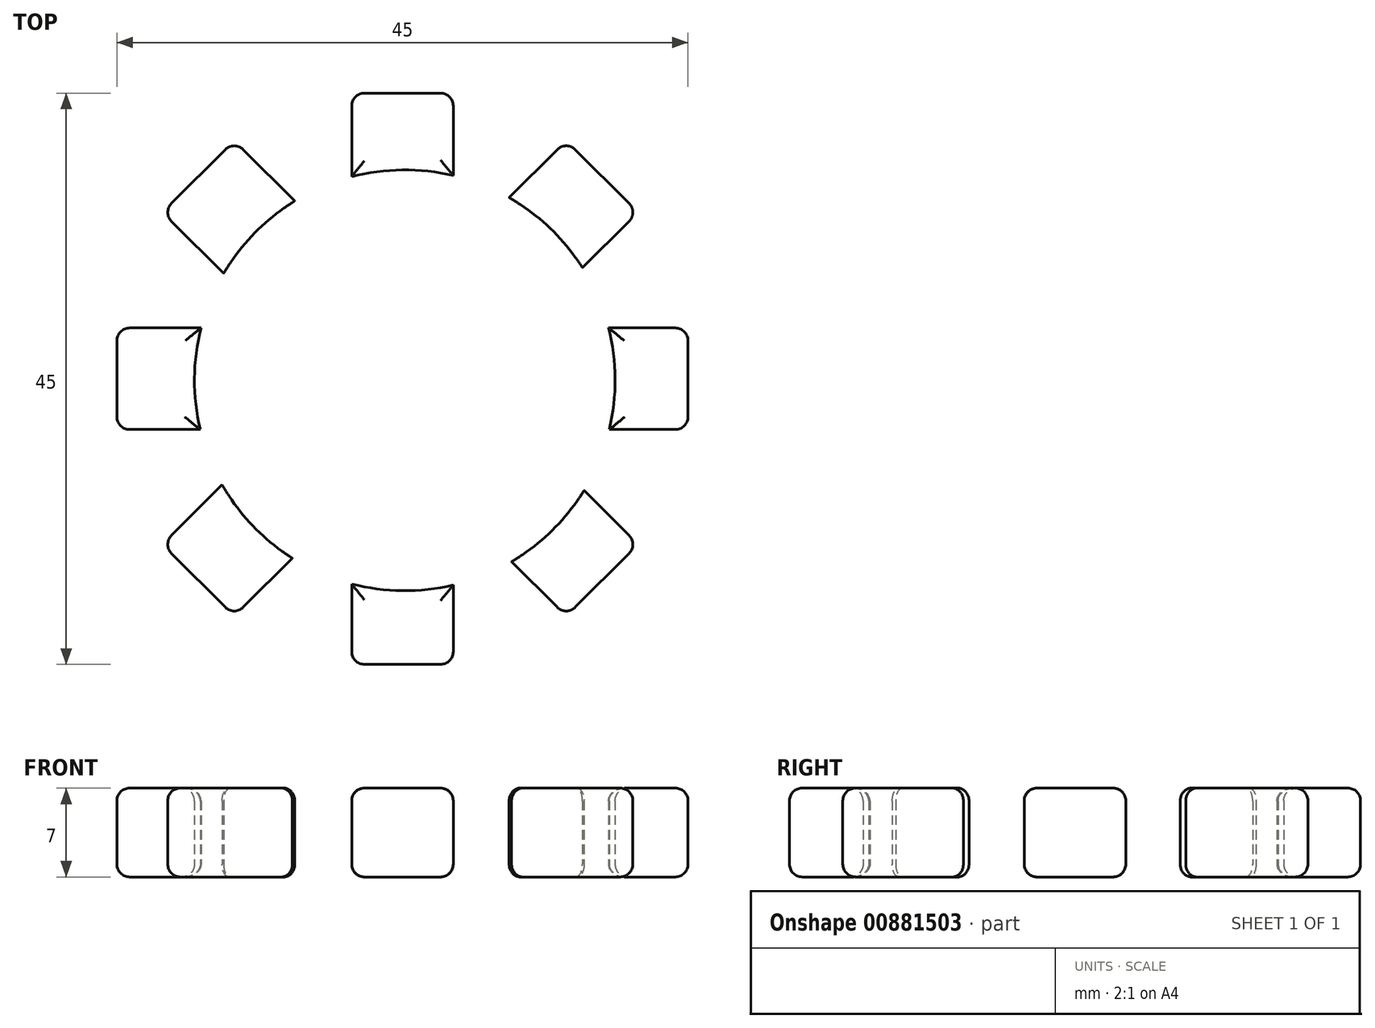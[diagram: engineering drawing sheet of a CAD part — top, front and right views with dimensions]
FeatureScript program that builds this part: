
annotation { "Feature Type Name" : "Feature", "Feature Type Description" : "" }
export const myFeature = defineFeature(function(context is Context, id is Id, definition is map)
    precondition{}
    {
        {
            var Q0;
            Q0=qCreatedBy(makeId("Top.planeOp"),FACE);
            var sketch = newSketch(context, id + "F0", { "sketchPlane" : qUnion([Q0])});
            skLineSegment(sketch, "E0.bottom", {"start": v(4, -22.5) * mm, "end": v(-4, -22.5) * mm});
            skLineSegment(sketch, "E0.top", {"start": v(4, 22.5) * mm, "end": v(-4, 22.5) * mm});
            skLineSegment(sketch, "E0.left", {"start": v(4, -22.5) * mm, "end": v(4, 22.5) * mm});
            skLineSegment(sketch, "E0.right", {"start": v(-4, -22.5) * mm, "end": v(-4, 22.5) * mm});
            skPoint(sketch, "E0.middle", {"position": v(0, 0) * mm});
            skLineSegment(sketch, "E1.bottom", {"start": v(22.5, -4) * mm, "end": v(-22.5, -4) * mm});
            skLineSegment(sketch, "E1.top", {"start": v(22.5, 4) * mm, "end": v(-22.5, 4) * mm});
            skLineSegment(sketch, "E1.left", {"start": v(22.5, -4) * mm, "end": v(22.5, 4) * mm});
            skLineSegment(sketch, "E1.right", {"start": v(-22.5, -4) * mm, "end": v(-22.5, 4) * mm});
            skPoint(sketch, "E2.middle", {"position": v(0.18, -0.13) * mm});
            skLineSegment(sketch, "E3.bottom", {"start": v(18.57, -13.06) * mm, "end": v(12.9, -18.71) * mm});
            skLineSegment(sketch, "E3.top", {"start": v(-13.25, 18.76) * mm, "end": v(-18.91, 13.1) * mm});
            skLineSegment(sketch, "E3.left", {"start": v(18.57, -13.06) * mm, "end": v(-13.25, 18.76) * mm});
            skLineSegment(sketch, "E3.right", {"start": v(12.9, -18.71) * mm, "end": v(-18.91, 13.1) * mm});
            skPoint(sketch, "E3.middle", {"position": v(-0.17, 0.03) * mm});
            skLineSegment(sketch, "E4.bottom", {"start": v(18.57, 13.1) * mm, "end": v(-13.25, -18.71) * mm});
            skLineSegment(sketch, "E4.top", {"start": v(12.9, 18.76) * mm, "end": v(-18.91, -13.06) * mm});
            skLineSegment(sketch, "E4.left", {"start": v(18.57, 13.1) * mm, "end": v(12.9, 18.76) * mm});
            skLineSegment(sketch, "E4.right", {"start": v(-13.25, -18.71) * mm, "end": v(-18.91, -13.06) * mm});
            skPoint(sketch, "E5.middle", {"position": v(0.05, 0.06) * mm});
            skCircle(sketch, "E6", {"center": v(-0.17, 0.03) * mm, "radius": 11.07 * mm});
            skCircle(sketch, "E7", {"center": v(0.18, -0.13) * mm, "radius": 16.57 * mm});
            skSolve(sketch);
        }
        {
            var Q0;
            {var subQ0=sQuery(id+"F0.wireOp",EDGE,"E3.top");Q0=makeQuery(id+"F0.imprint","IMPRINT",FACE,{"disambiguationData":[TD([[makeQuery(id+"F0.imprint","IMPRINT",EDGE,{"derivedFrom":subQ0}),1.0]])]});}
            var Q1;
            {var subQ0=sQuery(id+"F0.wireOp",EDGE,"E7");var subQ1=sQuery(id+"F0.wireOp",EDGE,"E3.left");var subQ2=makeQuery(id+"F0.imprint","INTERSECT",VERTEX,{"disambiguationData":[OD(1.0)],"derivedFrom":[subQ1,subQ0]});Q1=makeQuery(id+"F0.imprint","IMPRINT",FACE,{"disambiguationData":[TD([[makeQuery(id+"F0.imprint","IMPRINT",EDGE,{"disambiguationData":[TD([[subQ2,1.0]])],"derivedFrom":subQ1}),1.0]])]});}
            var Q2;
            {var subQ0=sQuery(id+"F0.wireOp",EDGE,"E7");var subQ1=sQuery(id+"F0.wireOp",EDGE,"E0.right");var subQ2=makeQuery(id+"F0.imprint","INTERSECT",VERTEX,{"disambiguationData":[OD(1.0)],"derivedFrom":[subQ1,subQ0]});Q2=makeQuery(id+"F0.imprint","IMPRINT",FACE,{"disambiguationData":[TD([[makeQuery(id+"F0.imprint","IMPRINT",EDGE,{"disambiguationData":[TD([[subQ2,1.0]])],"derivedFrom":subQ1}),1.0]])]});}
            var Q3;
            {var subQ0=sQuery(id+"F0.wireOp",EDGE,"E7");var subQ1=sQuery(id+"F0.wireOp",EDGE,"E0.left");var subQ2=makeQuery(id+"F0.imprint","INTERSECT",VERTEX,{"disambiguationData":[OD(1.0)],"derivedFrom":[subQ1,subQ0]});Q3=makeQuery(id+"F0.imprint","IMPRINT",FACE,{"disambiguationData":[TD([[makeQuery(id+"F0.imprint","IMPRINT",EDGE,{"disambiguationData":[TD([[subQ2,1.0]])],"derivedFrom":subQ1}),1.0]])]});}
            var Q4;
            {var subQ0=sQuery(id+"F0.wireOp",EDGE,"E0.top");Q4=makeQuery(id+"F0.imprint","IMPRINT",FACE,{"disambiguationData":[TD([[makeQuery(id+"F0.imprint","IMPRINT",EDGE,{"derivedFrom":subQ0}),1.0]])]});}
            var Q5;
            {var subQ0=sQuery(id+"F0.wireOp",EDGE,"E7");var subQ1=sQuery(id+"F0.wireOp",EDGE,"E0.left");var subQ2=makeQuery(id+"F0.imprint","INTERSECT",VERTEX,{"disambiguationData":[OD(1.0)],"derivedFrom":[subQ1,subQ0]});Q5=makeQuery(id+"F0.imprint","IMPRINT",FACE,{"disambiguationData":[TD([[makeQuery(id+"F0.imprint","IMPRINT",EDGE,{"disambiguationData":[TD([[subQ2,1.0]])],"derivedFrom":subQ1}),-1.0]])]});}
            var Q6;
            {var subQ0=sQuery(id+"F0.wireOp",EDGE,"E7");var subQ1=sQuery(id+"F0.wireOp",EDGE,"E4.bottom");var subQ2=makeQuery(id+"F0.imprint","INTERSECT",VERTEX,{"disambiguationData":[OD(0.0)],"derivedFrom":[subQ1,subQ0]});Q6=makeQuery(id+"F0.imprint","IMPRINT",FACE,{"disambiguationData":[TD([[makeQuery(id+"F0.imprint","IMPRINT",EDGE,{"disambiguationData":[TD([[subQ2,-1.0]])],"derivedFrom":subQ1}),-1.0]])]});}
            var Q7;
            {var subQ0=sQuery(id+"F0.wireOp",EDGE,"E4.left");Q7=makeQuery(id+"F0.imprint","IMPRINT",FACE,{"disambiguationData":[TD([[makeQuery(id+"F0.imprint","IMPRINT",EDGE,{"derivedFrom":subQ0}),1.0]])]});}
            var Q8;
            {var subQ0=sQuery(id+"F0.wireOp",EDGE,"E7");var subQ1=sQuery(id+"F0.wireOp",EDGE,"E1.top");var subQ2=makeQuery(id+"F0.imprint","INTERSECT",VERTEX,{"disambiguationData":[OD(0.0)],"derivedFrom":[subQ1,subQ0]});Q8=makeQuery(id+"F0.imprint","IMPRINT",FACE,{"disambiguationData":[TD([[makeQuery(id+"F0.imprint","IMPRINT",EDGE,{"disambiguationData":[TD([[subQ2,-1.0]])],"derivedFrom":subQ1}),-1.0]])]});}
            var Q9;
            {var subQ0=sQuery(id+"F0.wireOp",EDGE,"E7");var subQ1=sQuery(id+"F0.wireOp",EDGE,"E1.bottom");var subQ2=makeQuery(id+"F0.imprint","INTERSECT",VERTEX,{"disambiguationData":[OD(0.0)],"derivedFrom":[subQ1,subQ0]});Q9=makeQuery(id+"F0.imprint","IMPRINT",FACE,{"disambiguationData":[TD([[makeQuery(id+"F0.imprint","IMPRINT",EDGE,{"disambiguationData":[TD([[subQ2,-1.0]])],"derivedFrom":subQ1}),-1.0]])]});}
            var Q10;
            {var subQ0=sQuery(id+"F0.wireOp",EDGE,"E1.left");Q10=makeQuery(id+"F0.imprint","IMPRINT",FACE,{"disambiguationData":[TD([[makeQuery(id+"F0.imprint","IMPRINT",EDGE,{"derivedFrom":subQ0}),1.0]])]});}
            var Q11;
            {var subQ0=sQuery(id+"F0.wireOp",EDGE,"E7");var subQ1=sQuery(id+"F0.wireOp",EDGE,"E1.bottom");var subQ2=makeQuery(id+"F0.imprint","INTERSECT",VERTEX,{"disambiguationData":[OD(0.0)],"derivedFrom":[subQ1,subQ0]});Q11=makeQuery(id+"F0.imprint","IMPRINT",FACE,{"disambiguationData":[TD([[makeQuery(id+"F0.imprint","IMPRINT",EDGE,{"disambiguationData":[TD([[subQ2,-1.0]])],"derivedFrom":subQ1}),1.0]])]});}
            var Q12;
            {var subQ0=sQuery(id+"F0.wireOp",EDGE,"E7");var subQ1=sQuery(id+"F0.wireOp",EDGE,"E3.left");var subQ2=makeQuery(id+"F0.imprint","INTERSECT",VERTEX,{"disambiguationData":[OD(0.0)],"derivedFrom":[subQ1,subQ0]});Q12=makeQuery(id+"F0.imprint","IMPRINT",FACE,{"disambiguationData":[TD([[makeQuery(id+"F0.imprint","IMPRINT",EDGE,{"disambiguationData":[TD([[subQ2,-1.0]])],"derivedFrom":subQ1}),1.0]])]});}
            var Q13;
            {var subQ0=sQuery(id+"F0.wireOp",EDGE,"E3.bottom");Q13=makeQuery(id+"F0.imprint","IMPRINT",FACE,{"disambiguationData":[TD([[makeQuery(id+"F0.imprint","IMPRINT",EDGE,{"derivedFrom":subQ0}),-1.0]])]});}
            var Q14;
            {var subQ0=sQuery(id+"F0.wireOp",EDGE,"E7");var subQ1=sQuery(id+"F0.wireOp",EDGE,"E0.left");var subQ2=makeQuery(id+"F0.imprint","INTERSECT",VERTEX,{"disambiguationData":[OD(0.0)],"derivedFrom":[subQ1,subQ0]});Q14=makeQuery(id+"F0.imprint","IMPRINT",FACE,{"disambiguationData":[TD([[makeQuery(id+"F0.imprint","IMPRINT",EDGE,{"disambiguationData":[TD([[subQ2,-1.0]])],"derivedFrom":subQ1}),1.0]])]});}
            var Q15;
            {var subQ0=sQuery(id+"F0.wireOp",EDGE,"E0.bottom");Q15=makeQuery(id+"F0.imprint","IMPRINT",FACE,{"disambiguationData":[TD([[makeQuery(id+"F0.imprint","IMPRINT",EDGE,{"derivedFrom":subQ0}),-1.0]])]});}
            var Q16;
            {var subQ0=sQuery(id+"F0.wireOp",EDGE,"E7");var subQ1=sQuery(id+"F0.wireOp",EDGE,"E0.left");var subQ2=makeQuery(id+"F0.imprint","INTERSECT",VERTEX,{"disambiguationData":[OD(0.0)],"derivedFrom":[subQ1,subQ0]});Q16=makeQuery(id+"F0.imprint","IMPRINT",FACE,{"disambiguationData":[TD([[makeQuery(id+"F0.imprint","IMPRINT",EDGE,{"disambiguationData":[TD([[subQ2,-1.0]])],"derivedFrom":subQ1}),-1.0]])]});}
            var Q17;
            {var subQ0=sQuery(id+"F0.wireOp",EDGE,"E7");var subQ1=sQuery(id+"F0.wireOp",EDGE,"E0.right");var subQ2=makeQuery(id+"F0.imprint","INTERSECT",VERTEX,{"disambiguationData":[OD(0.0)],"derivedFrom":[subQ1,subQ0]});Q17=makeQuery(id+"F0.imprint","IMPRINT",FACE,{"disambiguationData":[TD([[makeQuery(id+"F0.imprint","IMPRINT",EDGE,{"disambiguationData":[TD([[subQ2,-1.0]])],"derivedFrom":subQ1}),1.0]])]});}
            var Q18;
            {var subQ0=sQuery(id+"F0.wireOp",EDGE,"E7");var subQ1=sQuery(id+"F0.wireOp",EDGE,"E4.bottom");var subQ2=makeQuery(id+"F0.imprint","INTERSECT",VERTEX,{"disambiguationData":[OD(1.0)],"derivedFrom":[subQ1,subQ0]});Q18=makeQuery(id+"F0.imprint","IMPRINT",FACE,{"disambiguationData":[TD([[makeQuery(id+"F0.imprint","IMPRINT",EDGE,{"disambiguationData":[TD([[subQ2,1.0]])],"derivedFrom":subQ1}),-1.0]])]});}
            var Q19;
            {var subQ0=sQuery(id+"F0.wireOp",EDGE,"E4.right");Q19=makeQuery(id+"F0.imprint","IMPRINT",FACE,{"disambiguationData":[TD([[makeQuery(id+"F0.imprint","IMPRINT",EDGE,{"derivedFrom":subQ0}),-1.0]])]});}
            var Q20;
            {var subQ0=sQuery(id+"F0.wireOp",EDGE,"E7");var subQ1=sQuery(id+"F0.wireOp",EDGE,"E1.bottom");var subQ2=makeQuery(id+"F0.imprint","INTERSECT",VERTEX,{"disambiguationData":[OD(1.0)],"derivedFrom":[subQ1,subQ0]});Q20=makeQuery(id+"F0.imprint","IMPRINT",FACE,{"disambiguationData":[TD([[makeQuery(id+"F0.imprint","IMPRINT",EDGE,{"disambiguationData":[TD([[subQ2,1.0]])],"derivedFrom":subQ1}),1.0]])]});}
            var Q21;
            {var subQ0=sQuery(id+"F0.wireOp",EDGE,"E7");var subQ1=sQuery(id+"F0.wireOp",EDGE,"E1.bottom");var subQ2=makeQuery(id+"F0.imprint","INTERSECT",VERTEX,{"disambiguationData":[OD(1.0)],"derivedFrom":[subQ1,subQ0]});Q21=makeQuery(id+"F0.imprint","IMPRINT",FACE,{"disambiguationData":[TD([[makeQuery(id+"F0.imprint","IMPRINT",EDGE,{"disambiguationData":[TD([[subQ2,1.0]])],"derivedFrom":subQ1}),-1.0]])]});}
            var Q22;
            {var subQ0=sQuery(id+"F0.wireOp",EDGE,"E1.right");Q22=makeQuery(id+"F0.imprint","IMPRINT",FACE,{"disambiguationData":[TD([[makeQuery(id+"F0.imprint","IMPRINT",EDGE,{"derivedFrom":subQ0}),-1.0]])]});}
            var Q23;
            {var subQ0=sQuery(id+"F0.wireOp",EDGE,"E7");var subQ1=sQuery(id+"F0.wireOp",EDGE,"E1.top");var subQ2=makeQuery(id+"F0.imprint","INTERSECT",VERTEX,{"disambiguationData":[OD(1.0)],"derivedFrom":[subQ1,subQ0]});Q23=makeQuery(id+"F0.imprint","IMPRINT",FACE,{"disambiguationData":[TD([[makeQuery(id+"F0.imprint","IMPRINT",EDGE,{"disambiguationData":[TD([[subQ2,1.0]])],"derivedFrom":subQ1}),-1.0]])]});}
            extrude(context, id + "F1", {"entities" : qUnion([Q0, Q1, Q2, Q3, Q4, Q5, Q6, Q7, Q8, Q9, Q10, Q11, Q12, Q13, Q14, Q15, Q16, Q17, Q18, Q19, Q20, Q21, Q22, Q23]), "depth" : 7 * mm, "offsetDistance" : 25 * mm});
        }
        {
            var Q0;
            {var subQ0=sQuery(id+"F0.wireOp",EDGE,"E3.left");Q0=makeQuery(id+"F1.opExtrude","CAP_EDGE",EDGE,{"disambiguationData":[OSD([subQ0]),TDD([makeQuery(id+"F0.imprint","IMPRINT",EDGE,{"disambiguationData":[TD([[makeQuery(id+"F0.imprint","INTERSECT",VERTEX,{"derivedFrom":[sQuery(id+"F0.wireOp",EDGE,"E3.top"),subQ0]}),1.0]])],"derivedFrom":subQ0})])],"isStart":false});}
            var Q1;
            {var subQ0=sQuery(id+"F0.wireOp",EDGE,"E7");Q1=makeQuery(id+"F1.opExtrude","CAP_EDGE",EDGE,{"disambiguationData":[OSD([subQ0]),TDD([makeQuery(id+"F0.imprint","IMPRINT",EDGE,{"disambiguationData":[TD([[makeQuery(id+"F0.imprint","INTERSECT",VERTEX,{"disambiguationData":[OD(1.0)],"derivedFrom":[sQuery(id+"F0.wireOp",EDGE,"E0.right"),subQ0]}),-1.0]])],"derivedFrom":subQ0})])],"isStart":false});}
            var Q2;
            {var subQ0=sQuery(id+"F0.wireOp",EDGE,"E0.right");Q2=makeQuery(id+"F1.opExtrude","CAP_EDGE",EDGE,{"disambiguationData":[OSD([subQ0]),TDD([makeQuery(id+"F0.imprint","IMPRINT",EDGE,{"disambiguationData":[TD([[makeQuery(id+"F0.imprint","INTERSECT",VERTEX,{"derivedFrom":[sQuery(id+"F0.wireOp",EDGE,"E0.top"),subQ0]}),1.0]])],"derivedFrom":subQ0})])],"isStart":false});}
            var Q3;
            {var subQ0=sQuery(id+"F0.wireOp",EDGE,"E0.left");Q3=makeQuery(id+"F1.opExtrude","CAP_EDGE",EDGE,{"disambiguationData":[OSD([subQ0]),TDD([makeQuery(id+"F0.imprint","IMPRINT",EDGE,{"disambiguationData":[TD([[makeQuery(id+"F0.imprint","INTERSECT",VERTEX,{"derivedFrom":[sQuery(id+"F0.wireOp",EDGE,"E0.top"),subQ0]}),1.0]])],"derivedFrom":subQ0})])],"isStart":false});}
            var Q4;
            {var subQ0=sQuery(id+"F0.wireOp",EDGE,"E7");Q4=makeQuery(id+"F1.opExtrude","CAP_EDGE",EDGE,{"disambiguationData":[OSD([subQ0]),TDD([makeQuery(id+"F0.imprint","IMPRINT",EDGE,{"disambiguationData":[TD([[makeQuery(id+"F0.imprint","INTERSECT",VERTEX,{"disambiguationData":[OD(1.0)],"derivedFrom":[sQuery(id+"F0.wireOp",EDGE,"E0.left"),subQ0]}),1.0]])],"derivedFrom":subQ0})])],"isStart":false});}
            var Q5;
            {var subQ0=sQuery(id+"F0.wireOp",EDGE,"E4.top");Q5=makeQuery(id+"F1.opExtrude","CAP_EDGE",EDGE,{"disambiguationData":[OSD([subQ0]),TDD([makeQuery(id+"F0.imprint","IMPRINT",EDGE,{"disambiguationData":[TD([[makeQuery(id+"F0.imprint","INTERSECT",VERTEX,{"derivedFrom":[subQ0,sQuery(id+"F0.wireOp",EDGE,"E4.left")]}),-1.0]])],"derivedFrom":subQ0})])],"isStart":false});}
            var Q6;
            {var subQ0=sQuery(id+"F0.wireOp",EDGE,"E4.bottom");Q6=makeQuery(id+"F1.opExtrude","CAP_EDGE",EDGE,{"disambiguationData":[OSD([subQ0]),TDD([makeQuery(id+"F0.imprint","IMPRINT",EDGE,{"disambiguationData":[TD([[makeQuery(id+"F0.imprint","INTERSECT",VERTEX,{"derivedFrom":[subQ0,sQuery(id+"F0.wireOp",EDGE,"E4.left")]}),-1.0]])],"derivedFrom":subQ0})])],"isStart":false});}
            var Q7;
            {var subQ0=sQuery(id+"F0.wireOp",EDGE,"E1.top");Q7=makeQuery(id+"F1.opExtrude","CAP_EDGE",EDGE,{"disambiguationData":[OSD([subQ0]),TDD([makeQuery(id+"F0.imprint","IMPRINT",EDGE,{"disambiguationData":[TD([[makeQuery(id+"F0.imprint","INTERSECT",VERTEX,{"derivedFrom":[subQ0,sQuery(id+"F0.wireOp",EDGE,"E1.left")]}),-1.0]])],"derivedFrom":subQ0})])],"isStart":false});}
            var Q8;
            {var subQ0=sQuery(id+"F0.wireOp",EDGE,"E1.bottom");Q8=makeQuery(id+"F1.opExtrude","CAP_EDGE",EDGE,{"disambiguationData":[OSD([subQ0]),TDD([makeQuery(id+"F0.imprint","IMPRINT",EDGE,{"disambiguationData":[TD([[makeQuery(id+"F0.imprint","INTERSECT",VERTEX,{"derivedFrom":[subQ0,sQuery(id+"F0.wireOp",EDGE,"E1.left")]}),-1.0]])],"derivedFrom":subQ0})])],"isStart":false});}
            var Q9;
            {var subQ0=sQuery(id+"F0.wireOp",EDGE,"E7");Q9=makeQuery(id+"F1.opExtrude","CAP_EDGE",EDGE,{"disambiguationData":[OSD([subQ0]),TDD([makeQuery(id+"F0.imprint","IMPRINT",EDGE,{"disambiguationData":[TD([[makeQuery(id+"F0.imprint","INTERSECT",VERTEX,{"disambiguationData":[OD(0.0)],"derivedFrom":[sQuery(id+"F0.wireOp",EDGE,"E1.top"),subQ0]}),-1.0]])],"derivedFrom":subQ0})])],"isStart":false});}
            var Q10;
            {var subQ0=sQuery(id+"F0.wireOp",EDGE,"E7");Q10=makeQuery(id+"F1.opExtrude","CAP_EDGE",EDGE,{"disambiguationData":[OSD([subQ0]),TDD([makeQuery(id+"F0.imprint","IMPRINT",EDGE,{"disambiguationData":[TD([[makeQuery(id+"F0.imprint","INTERSECT",VERTEX,{"disambiguationData":[OD(0.0)],"derivedFrom":[sQuery(id+"F0.wireOp",EDGE,"E1.bottom"),subQ0]}),1.0]])],"derivedFrom":subQ0})])],"isStart":false});}
            var Q11;
            {var subQ0=sQuery(id+"F0.wireOp",EDGE,"E3.left");Q11=makeQuery(id+"F1.opExtrude","CAP_EDGE",EDGE,{"disambiguationData":[OSD([subQ0]),TDD([makeQuery(id+"F0.imprint","IMPRINT",EDGE,{"disambiguationData":[TD([[makeQuery(id+"F0.imprint","INTERSECT",VERTEX,{"derivedFrom":[sQuery(id+"F0.wireOp",EDGE,"E3.bottom"),subQ0]}),-1.0]])],"derivedFrom":subQ0})])],"isStart":false});}
            var Q12;
            {var subQ0=sQuery(id+"F0.wireOp",EDGE,"E3.right");Q12=makeQuery(id+"F1.opExtrude","CAP_EDGE",EDGE,{"disambiguationData":[OSD([subQ0]),TDD([makeQuery(id+"F0.imprint","IMPRINT",EDGE,{"disambiguationData":[TD([[makeQuery(id+"F0.imprint","INTERSECT",VERTEX,{"derivedFrom":[sQuery(id+"F0.wireOp",EDGE,"E3.bottom"),subQ0]}),-1.0]])],"derivedFrom":subQ0})])],"isStart":false});}
            var Q13;
            {var subQ0=sQuery(id+"F0.wireOp",EDGE,"E7");Q13=makeQuery(id+"F1.opExtrude","CAP_EDGE",EDGE,{"disambiguationData":[OSD([subQ0]),TDD([makeQuery(id+"F0.imprint","IMPRINT",EDGE,{"disambiguationData":[TD([[makeQuery(id+"F0.imprint","INTERSECT",VERTEX,{"disambiguationData":[OD(0.0)],"derivedFrom":[sQuery(id+"F0.wireOp",EDGE,"E0.left"),subQ0]}),-1.0]])],"derivedFrom":subQ0})])],"isStart":false});}
            var Q14;
            {var subQ0=sQuery(id+"F0.wireOp",EDGE,"E0.left");Q14=makeQuery(id+"F1.opExtrude","CAP_EDGE",EDGE,{"disambiguationData":[OSD([subQ0]),TDD([makeQuery(id+"F0.imprint","IMPRINT",EDGE,{"disambiguationData":[TD([[makeQuery(id+"F0.imprint","INTERSECT",VERTEX,{"derivedFrom":[sQuery(id+"F0.wireOp",EDGE,"E0.bottom"),subQ0]}),-1.0]])],"derivedFrom":subQ0})])],"isStart":false});}
            var Q15;
            {var subQ0=sQuery(id+"F0.wireOp",EDGE,"E0.right");Q15=makeQuery(id+"F1.opExtrude","CAP_EDGE",EDGE,{"disambiguationData":[OSD([subQ0]),TDD([makeQuery(id+"F0.imprint","IMPRINT",EDGE,{"disambiguationData":[TD([[makeQuery(id+"F0.imprint","INTERSECT",VERTEX,{"derivedFrom":[sQuery(id+"F0.wireOp",EDGE,"E0.bottom"),subQ0]}),-1.0]])],"derivedFrom":subQ0})])],"isStart":false});}
            var Q16;
            {var subQ0=sQuery(id+"F0.wireOp",EDGE,"E7");Q16=makeQuery(id+"F1.opExtrude","CAP_EDGE",EDGE,{"disambiguationData":[OSD([subQ0]),TDD([makeQuery(id+"F0.imprint","IMPRINT",EDGE,{"disambiguationData":[TD([[makeQuery(id+"F0.imprint","INTERSECT",VERTEX,{"disambiguationData":[OD(0.0)],"derivedFrom":[sQuery(id+"F0.wireOp",EDGE,"E0.right"),subQ0]}),1.0]])],"derivedFrom":subQ0})])],"isStart":false});}
            var Q17;
            {var subQ0=sQuery(id+"F0.wireOp",EDGE,"E4.bottom");Q17=makeQuery(id+"F1.opExtrude","CAP_EDGE",EDGE,{"disambiguationData":[OSD([subQ0]),TDD([makeQuery(id+"F0.imprint","IMPRINT",EDGE,{"disambiguationData":[TD([[makeQuery(id+"F0.imprint","INTERSECT",VERTEX,{"derivedFrom":[subQ0,sQuery(id+"F0.wireOp",EDGE,"E4.right")]}),1.0]])],"derivedFrom":subQ0})])],"isStart":false});}
            var Q18;
            {var subQ0=sQuery(id+"F0.wireOp",EDGE,"E4.top");Q18=makeQuery(id+"F1.opExtrude","CAP_EDGE",EDGE,{"disambiguationData":[OSD([subQ0]),TDD([makeQuery(id+"F0.imprint","IMPRINT",EDGE,{"disambiguationData":[TD([[makeQuery(id+"F0.imprint","INTERSECT",VERTEX,{"derivedFrom":[subQ0,sQuery(id+"F0.wireOp",EDGE,"E4.right")]}),1.0]])],"derivedFrom":subQ0})])],"isStart":false});}
            var Q19;
            {var subQ0=sQuery(id+"F0.wireOp",EDGE,"E7");Q19=makeQuery(id+"F1.opExtrude","CAP_EDGE",EDGE,{"disambiguationData":[OSD([subQ0]),TDD([makeQuery(id+"F0.imprint","IMPRINT",EDGE,{"disambiguationData":[TD([[makeQuery(id+"F0.imprint","INTERSECT",VERTEX,{"disambiguationData":[OD(1.0)],"derivedFrom":[sQuery(id+"F0.wireOp",EDGE,"E1.bottom"),subQ0]}),-1.0]])],"derivedFrom":subQ0})])],"isStart":false});}
            var Q20;
            {var subQ0=sQuery(id+"F0.wireOp",EDGE,"E1.bottom");Q20=makeQuery(id+"F1.opExtrude","CAP_EDGE",EDGE,{"disambiguationData":[OSD([subQ0]),TDD([makeQuery(id+"F0.imprint","IMPRINT",EDGE,{"disambiguationData":[TD([[makeQuery(id+"F0.imprint","INTERSECT",VERTEX,{"derivedFrom":[subQ0,sQuery(id+"F0.wireOp",EDGE,"E1.right")]}),1.0]])],"derivedFrom":subQ0})])],"isStart":false});}
            var Q21;
            {var subQ0=sQuery(id+"F0.wireOp",EDGE,"E1.top");Q21=makeQuery(id+"F1.opExtrude","CAP_EDGE",EDGE,{"disambiguationData":[OSD([subQ0]),TDD([makeQuery(id+"F0.imprint","IMPRINT",EDGE,{"disambiguationData":[TD([[makeQuery(id+"F0.imprint","INTERSECT",VERTEX,{"derivedFrom":[subQ0,sQuery(id+"F0.wireOp",EDGE,"E1.right")]}),1.0]])],"derivedFrom":subQ0})])],"isStart":false});}
            var Q22;
            {var subQ0=sQuery(id+"F0.wireOp",EDGE,"E7");Q22=makeQuery(id+"F1.opExtrude","CAP_EDGE",EDGE,{"disambiguationData":[OSD([subQ0]),TDD([makeQuery(id+"F0.imprint","IMPRINT",EDGE,{"disambiguationData":[TD([[makeQuery(id+"F0.imprint","INTERSECT",VERTEX,{"disambiguationData":[OD(1.0)],"derivedFrom":[sQuery(id+"F0.wireOp",EDGE,"E1.top"),subQ0]}),1.0]])],"derivedFrom":subQ0})])],"isStart":false});}
            var Q23;
            {var subQ0=sQuery(id+"F0.wireOp",EDGE,"E3.right");Q23=makeQuery(id+"F1.opExtrude","CAP_EDGE",EDGE,{"disambiguationData":[OSD([subQ0]),TDD([makeQuery(id+"F0.imprint","IMPRINT",EDGE,{"disambiguationData":[TD([[makeQuery(id+"F0.imprint","INTERSECT",VERTEX,{"derivedFrom":[sQuery(id+"F0.wireOp",EDGE,"E3.top"),subQ0]}),1.0]])],"derivedFrom":subQ0})])],"isStart":false});}
            fillet(context, id + "F2", {"entities" : qUnion([Q0, Q1, Q2, Q3, Q4, Q5, Q6, Q7, Q8, Q9, Q10, Q11, Q12, Q13, Q14, Q15, Q16, Q17, Q18, Q19, Q20, Q21, Q22, Q23]), "radius" : 1 * mm, "tangentPropagation" : true, "allowEdgeOverflow" : false});
        }
        {
            var Q0;
            {var subQ0=sQuery(id+"F0.wireOp",EDGE,"E3.left");Q0=makeQuery(id+"F1.opExtrude","CAP_EDGE",EDGE,{"disambiguationData":[OSD([subQ0]),TDD([makeQuery(id+"F0.imprint","IMPRINT",EDGE,{"disambiguationData":[TD([[makeQuery(id+"F0.imprint","INTERSECT",VERTEX,{"derivedFrom":[sQuery(id+"F0.wireOp",EDGE,"E3.bottom"),subQ0]}),-1.0]])],"derivedFrom":subQ0})])],"isStart":true});}
            var Q1;
            {var subQ0=sQuery(id+"F0.wireOp",EDGE,"E3.right");Q1=makeQuery(id+"F1.opExtrude","CAP_EDGE",EDGE,{"disambiguationData":[OSD([subQ0]),TDD([makeQuery(id+"F0.imprint","IMPRINT",EDGE,{"disambiguationData":[TD([[makeQuery(id+"F0.imprint","INTERSECT",VERTEX,{"derivedFrom":[sQuery(id+"F0.wireOp",EDGE,"E3.bottom"),subQ0]}),-1.0]])],"derivedFrom":subQ0})])],"isStart":true});}
            var Q2;
            {var subQ0=sQuery(id+"F0.wireOp",EDGE,"E7");Q2=makeQuery(id+"F1.opExtrude","CAP_EDGE",EDGE,{"disambiguationData":[OSD([subQ0]),TDD([makeQuery(id+"F0.imprint","IMPRINT",EDGE,{"disambiguationData":[TD([[makeQuery(id+"F0.imprint","INTERSECT",VERTEX,{"disambiguationData":[OD(0.0)],"derivedFrom":[sQuery(id+"F0.wireOp",EDGE,"E1.bottom"),subQ0]}),1.0]])],"derivedFrom":subQ0})])],"isStart":true});}
            var Q3;
            {var subQ0=sQuery(id+"F0.wireOp",EDGE,"E7");Q3=makeQuery(id+"F1.opExtrude","CAP_EDGE",EDGE,{"disambiguationData":[OSD([subQ0]),TDD([makeQuery(id+"F0.imprint","IMPRINT",EDGE,{"disambiguationData":[TD([[makeQuery(id+"F0.imprint","INTERSECT",VERTEX,{"disambiguationData":[OD(0.0)],"derivedFrom":[sQuery(id+"F0.wireOp",EDGE,"E0.left"),subQ0]}),-1.0]])],"derivedFrom":subQ0})])],"isStart":true});}
            var Q4;
            {var subQ0=sQuery(id+"F0.wireOp",EDGE,"E0.left");Q4=makeQuery(id+"F1.opExtrude","CAP_EDGE",EDGE,{"disambiguationData":[OSD([subQ0]),TDD([makeQuery(id+"F0.imprint","IMPRINT",EDGE,{"disambiguationData":[TD([[makeQuery(id+"F0.imprint","INTERSECT",VERTEX,{"derivedFrom":[sQuery(id+"F0.wireOp",EDGE,"E0.bottom"),subQ0]}),-1.0]])],"derivedFrom":subQ0})])],"isStart":true});}
            var Q5;
            {var subQ0=sQuery(id+"F0.wireOp",EDGE,"E0.right");Q5=makeQuery(id+"F1.opExtrude","CAP_EDGE",EDGE,{"disambiguationData":[OSD([subQ0]),TDD([makeQuery(id+"F0.imprint","IMPRINT",EDGE,{"disambiguationData":[TD([[makeQuery(id+"F0.imprint","INTERSECT",VERTEX,{"derivedFrom":[sQuery(id+"F0.wireOp",EDGE,"E0.bottom"),subQ0]}),-1.0]])],"derivedFrom":subQ0})])],"isStart":true});}
            var Q6;
            {var subQ0=sQuery(id+"F0.wireOp",EDGE,"E7");Q6=makeQuery(id+"F1.opExtrude","CAP_EDGE",EDGE,{"disambiguationData":[OSD([subQ0]),TDD([makeQuery(id+"F0.imprint","IMPRINT",EDGE,{"disambiguationData":[TD([[makeQuery(id+"F0.imprint","INTERSECT",VERTEX,{"disambiguationData":[OD(0.0)],"derivedFrom":[sQuery(id+"F0.wireOp",EDGE,"E0.right"),subQ0]}),1.0]])],"derivedFrom":subQ0})])],"isStart":true});}
            var Q7;
            {var subQ0=sQuery(id+"F0.wireOp",EDGE,"E4.bottom");Q7=makeQuery(id+"F1.opExtrude","CAP_EDGE",EDGE,{"disambiguationData":[OSD([subQ0]),TDD([makeQuery(id+"F0.imprint","IMPRINT",EDGE,{"disambiguationData":[TD([[makeQuery(id+"F0.imprint","INTERSECT",VERTEX,{"derivedFrom":[subQ0,sQuery(id+"F0.wireOp",EDGE,"E4.right")]}),1.0]])],"derivedFrom":subQ0})])],"isStart":true});}
            var Q8;
            {var subQ0=sQuery(id+"F0.wireOp",EDGE,"E4.top");Q8=makeQuery(id+"F1.opExtrude","CAP_EDGE",EDGE,{"disambiguationData":[OSD([subQ0]),TDD([makeQuery(id+"F0.imprint","IMPRINT",EDGE,{"disambiguationData":[TD([[makeQuery(id+"F0.imprint","INTERSECT",VERTEX,{"derivedFrom":[subQ0,sQuery(id+"F0.wireOp",EDGE,"E4.right")]}),1.0]])],"derivedFrom":subQ0})])],"isStart":true});}
            var Q9;
            {var subQ0=sQuery(id+"F0.wireOp",EDGE,"E7");Q9=makeQuery(id+"F1.opExtrude","CAP_EDGE",EDGE,{"disambiguationData":[OSD([subQ0]),TDD([makeQuery(id+"F0.imprint","IMPRINT",EDGE,{"disambiguationData":[TD([[makeQuery(id+"F0.imprint","INTERSECT",VERTEX,{"disambiguationData":[OD(1.0)],"derivedFrom":[sQuery(id+"F0.wireOp",EDGE,"E1.bottom"),subQ0]}),-1.0]])],"derivedFrom":subQ0})])],"isStart":true});}
            var Q10;
            {var subQ0=sQuery(id+"F0.wireOp",EDGE,"E1.bottom");Q10=makeQuery(id+"F1.opExtrude","CAP_EDGE",EDGE,{"disambiguationData":[OSD([subQ0]),TDD([makeQuery(id+"F0.imprint","IMPRINT",EDGE,{"disambiguationData":[TD([[makeQuery(id+"F0.imprint","INTERSECT",VERTEX,{"derivedFrom":[subQ0,sQuery(id+"F0.wireOp",EDGE,"E1.right")]}),1.0]])],"derivedFrom":subQ0})])],"isStart":true});}
            var Q11;
            {var subQ0=sQuery(id+"F0.wireOp",EDGE,"E1.top");Q11=makeQuery(id+"F1.opExtrude","CAP_EDGE",EDGE,{"disambiguationData":[OSD([subQ0]),TDD([makeQuery(id+"F0.imprint","IMPRINT",EDGE,{"disambiguationData":[TD([[makeQuery(id+"F0.imprint","INTERSECT",VERTEX,{"derivedFrom":[subQ0,sQuery(id+"F0.wireOp",EDGE,"E1.right")]}),1.0]])],"derivedFrom":subQ0})])],"isStart":true});}
            var Q12;
            {var subQ0=sQuery(id+"F0.wireOp",EDGE,"E7");Q12=makeQuery(id+"F1.opExtrude","CAP_EDGE",EDGE,{"disambiguationData":[OSD([subQ0]),TDD([makeQuery(id+"F0.imprint","IMPRINT",EDGE,{"disambiguationData":[TD([[makeQuery(id+"F0.imprint","INTERSECT",VERTEX,{"disambiguationData":[OD(1.0)],"derivedFrom":[sQuery(id+"F0.wireOp",EDGE,"E1.top"),subQ0]}),1.0]])],"derivedFrom":subQ0})])],"isStart":true});}
            var Q13;
            {var subQ0=sQuery(id+"F0.wireOp",EDGE,"E3.right");Q13=makeQuery(id+"F1.opExtrude","CAP_EDGE",EDGE,{"disambiguationData":[OSD([subQ0]),TDD([makeQuery(id+"F0.imprint","IMPRINT",EDGE,{"disambiguationData":[TD([[makeQuery(id+"F0.imprint","INTERSECT",VERTEX,{"derivedFrom":[sQuery(id+"F0.wireOp",EDGE,"E3.top"),subQ0]}),1.0]])],"derivedFrom":subQ0})])],"isStart":true});}
            var Q14;
            {var subQ0=sQuery(id+"F0.wireOp",EDGE,"E3.left");Q14=makeQuery(id+"F1.opExtrude","CAP_EDGE",EDGE,{"disambiguationData":[OSD([subQ0]),TDD([makeQuery(id+"F0.imprint","IMPRINT",EDGE,{"disambiguationData":[TD([[makeQuery(id+"F0.imprint","INTERSECT",VERTEX,{"derivedFrom":[sQuery(id+"F0.wireOp",EDGE,"E3.top"),subQ0]}),1.0]])],"derivedFrom":subQ0})])],"isStart":true});}
            var Q15;
            {var subQ0=sQuery(id+"F0.wireOp",EDGE,"E7");Q15=makeQuery(id+"F1.opExtrude","CAP_EDGE",EDGE,{"disambiguationData":[OSD([subQ0]),TDD([makeQuery(id+"F0.imprint","IMPRINT",EDGE,{"disambiguationData":[TD([[makeQuery(id+"F0.imprint","INTERSECT",VERTEX,{"disambiguationData":[OD(1.0)],"derivedFrom":[sQuery(id+"F0.wireOp",EDGE,"E0.right"),subQ0]}),-1.0]])],"derivedFrom":subQ0})])],"isStart":true});}
            var Q16;
            {var subQ0=sQuery(id+"F0.wireOp",EDGE,"E0.right");Q16=makeQuery(id+"F1.opExtrude","CAP_EDGE",EDGE,{"disambiguationData":[OSD([subQ0]),TDD([makeQuery(id+"F0.imprint","IMPRINT",EDGE,{"disambiguationData":[TD([[makeQuery(id+"F0.imprint","INTERSECT",VERTEX,{"derivedFrom":[sQuery(id+"F0.wireOp",EDGE,"E0.top"),subQ0]}),1.0]])],"derivedFrom":subQ0})])],"isStart":true});}
            var Q17;
            {var subQ0=sQuery(id+"F0.wireOp",EDGE,"E0.left");Q17=makeQuery(id+"F1.opExtrude","CAP_EDGE",EDGE,{"disambiguationData":[OSD([subQ0]),TDD([makeQuery(id+"F0.imprint","IMPRINT",EDGE,{"disambiguationData":[TD([[makeQuery(id+"F0.imprint","INTERSECT",VERTEX,{"derivedFrom":[sQuery(id+"F0.wireOp",EDGE,"E0.top"),subQ0]}),1.0]])],"derivedFrom":subQ0})])],"isStart":true});}
            var Q18;
            {var subQ0=sQuery(id+"F0.wireOp",EDGE,"E7");Q18=makeQuery(id+"F1.opExtrude","CAP_EDGE",EDGE,{"disambiguationData":[OSD([subQ0]),TDD([makeQuery(id+"F0.imprint","IMPRINT",EDGE,{"disambiguationData":[TD([[makeQuery(id+"F0.imprint","INTERSECT",VERTEX,{"disambiguationData":[OD(1.0)],"derivedFrom":[sQuery(id+"F0.wireOp",EDGE,"E0.left"),subQ0]}),1.0]])],"derivedFrom":subQ0})])],"isStart":true});}
            var Q19;
            {var subQ0=sQuery(id+"F0.wireOp",EDGE,"E4.top");Q19=makeQuery(id+"F1.opExtrude","CAP_EDGE",EDGE,{"disambiguationData":[OSD([subQ0]),TDD([makeQuery(id+"F0.imprint","IMPRINT",EDGE,{"disambiguationData":[TD([[makeQuery(id+"F0.imprint","INTERSECT",VERTEX,{"derivedFrom":[subQ0,sQuery(id+"F0.wireOp",EDGE,"E4.left")]}),-1.0]])],"derivedFrom":subQ0})])],"isStart":true});}
            var Q20;
            {var subQ0=sQuery(id+"F0.wireOp",EDGE,"E4.bottom");Q20=makeQuery(id+"F1.opExtrude","CAP_EDGE",EDGE,{"disambiguationData":[OSD([subQ0]),TDD([makeQuery(id+"F0.imprint","IMPRINT",EDGE,{"disambiguationData":[TD([[makeQuery(id+"F0.imprint","INTERSECT",VERTEX,{"derivedFrom":[subQ0,sQuery(id+"F0.wireOp",EDGE,"E4.left")]}),-1.0]])],"derivedFrom":subQ0})])],"isStart":true});}
            var Q21;
            {var subQ0=sQuery(id+"F0.wireOp",EDGE,"E7");Q21=makeQuery(id+"F1.opExtrude","CAP_EDGE",EDGE,{"disambiguationData":[OSD([subQ0]),TDD([makeQuery(id+"F0.imprint","IMPRINT",EDGE,{"disambiguationData":[TD([[makeQuery(id+"F0.imprint","INTERSECT",VERTEX,{"disambiguationData":[OD(0.0)],"derivedFrom":[sQuery(id+"F0.wireOp",EDGE,"E1.top"),subQ0]}),-1.0]])],"derivedFrom":subQ0})])],"isStart":true});}
            var Q22;
            {var subQ0=sQuery(id+"F0.wireOp",EDGE,"E1.top");Q22=makeQuery(id+"F1.opExtrude","CAP_EDGE",EDGE,{"disambiguationData":[OSD([subQ0]),TDD([makeQuery(id+"F0.imprint","IMPRINT",EDGE,{"disambiguationData":[TD([[makeQuery(id+"F0.imprint","INTERSECT",VERTEX,{"derivedFrom":[subQ0,sQuery(id+"F0.wireOp",EDGE,"E1.left")]}),-1.0]])],"derivedFrom":subQ0})])],"isStart":true});}
            var Q23;
            {var subQ0=sQuery(id+"F0.wireOp",EDGE,"E1.bottom");Q23=makeQuery(id+"F1.opExtrude","CAP_EDGE",EDGE,{"disambiguationData":[OSD([subQ0]),TDD([makeQuery(id+"F0.imprint","IMPRINT",EDGE,{"disambiguationData":[TD([[makeQuery(id+"F0.imprint","INTERSECT",VERTEX,{"derivedFrom":[subQ0,sQuery(id+"F0.wireOp",EDGE,"E1.left")]}),-1.0]])],"derivedFrom":subQ0})])],"isStart":true});}
            fillet(context, id + "F3", {"entities" : qUnion([Q0, Q1, Q2, Q3, Q4, Q5, Q6, Q7, Q8, Q9, Q10, Q11, Q12, Q13, Q14, Q15, Q16, Q17, Q18, Q19, Q20, Q21, Q22, Q23]), "radius" : 1 * mm, "tangentPropagation" : true, "allowEdgeOverflow" : false});
        }
        {
            var Q0;
            Q0=makeQuery(id+"F1.opExtrude","CAP_EDGE",EDGE,{"disambiguationData":[OSD([sQuery(id+"F0.wireOp",EDGE,"E3.bottom")])],"isStart":false});
            var Q1;
            Q1=makeQuery(id+"F1.opExtrude","CAP_EDGE",EDGE,{"disambiguationData":[OSD([sQuery(id+"F0.wireOp",EDGE,"E3.bottom")])],"isStart":true});
            var Q2;
            Q2=makeQuery(id+"F1.opExtrude","SWEPT_EDGE",EDGE,{"disambiguationData":[OSD([sQuery(id+"F0.wireOp",EDGE,"E3.bottom"),sQuery(id+"F0.wireOp",EDGE,"E3.right")])]});
            var Q3;
            Q3=makeQuery(id+"F1.opExtrude","SWEPT_EDGE",EDGE,{"disambiguationData":[OSD([sQuery(id+"F0.wireOp",EDGE,"E3.bottom"),sQuery(id+"F0.wireOp",EDGE,"E3.left")])]});
            var Q4;
            Q4=makeQuery(id+"F1.opExtrude","CAP_EDGE",EDGE,{"disambiguationData":[OSD([sQuery(id+"F0.wireOp",EDGE,"E0.bottom")])],"isStart":false});
            var Q5;
            Q5=makeQuery(id+"F1.opExtrude","CAP_EDGE",EDGE,{"disambiguationData":[OSD([sQuery(id+"F0.wireOp",EDGE,"E0.bottom")])],"isStart":true});
            var Q6;
            Q6=makeQuery(id+"F1.opExtrude","SWEPT_EDGE",EDGE,{"disambiguationData":[OSD([sQuery(id+"F0.wireOp",EDGE,"E0.bottom"),sQuery(id+"F0.wireOp",EDGE,"E0.right")])]});
            var Q7;
            Q7=makeQuery(id+"F1.opExtrude","SWEPT_EDGE",EDGE,{"disambiguationData":[OSD([sQuery(id+"F0.wireOp",EDGE,"E0.bottom"),sQuery(id+"F0.wireOp",EDGE,"E0.left")])]});
            var Q8;
            Q8=makeQuery(id+"F1.opExtrude","SWEPT_EDGE",EDGE,{"disambiguationData":[OSD([sQuery(id+"F0.wireOp",EDGE,"E4.bottom"),sQuery(id+"F0.wireOp",EDGE,"E4.right")])]});
            var Q9;
            Q9=makeQuery(id+"F1.opExtrude","CAP_EDGE",EDGE,{"disambiguationData":[OSD([sQuery(id+"F0.wireOp",EDGE,"E4.right")])],"isStart":false});
            var Q10;
            Q10=makeQuery(id+"F1.opExtrude","CAP_EDGE",EDGE,{"disambiguationData":[OSD([sQuery(id+"F0.wireOp",EDGE,"E4.right")])],"isStart":true});
            var Q11;
            Q11=makeQuery(id+"F1.opExtrude","SWEPT_EDGE",EDGE,{"disambiguationData":[OSD([sQuery(id+"F0.wireOp",EDGE,"E4.top"),sQuery(id+"F0.wireOp",EDGE,"E4.right")])]});
            var Q12;
            Q12=makeQuery(id+"F1.opExtrude","SWEPT_EDGE",EDGE,{"disambiguationData":[OSD([sQuery(id+"F0.wireOp",EDGE,"E1.top"),sQuery(id+"F0.wireOp",EDGE,"E1.right")])]});
            var Q13;
            Q13=makeQuery(id+"F1.opExtrude","CAP_EDGE",EDGE,{"disambiguationData":[OSD([sQuery(id+"F0.wireOp",EDGE,"E1.right")])],"isStart":false});
            var Q14;
            Q14=makeQuery(id+"F1.opExtrude","SWEPT_EDGE",EDGE,{"disambiguationData":[OSD([sQuery(id+"F0.wireOp",EDGE,"E1.bottom"),sQuery(id+"F0.wireOp",EDGE,"E1.right")])]});
            var Q15;
            Q15=makeQuery(id+"F1.opExtrude","CAP_EDGE",EDGE,{"disambiguationData":[OSD([sQuery(id+"F0.wireOp",EDGE,"E1.right")])],"isStart":true});
            var Q16;
            Q16=makeQuery(id+"F1.opExtrude","SWEPT_EDGE",EDGE,{"disambiguationData":[OSD([sQuery(id+"F0.wireOp",EDGE,"E3.top"),sQuery(id+"F0.wireOp",EDGE,"E3.right")])]});
            var Q17;
            Q17=makeQuery(id+"F1.opExtrude","SWEPT_EDGE",EDGE,{"disambiguationData":[OSD([sQuery(id+"F0.wireOp",EDGE,"E3.top"),sQuery(id+"F0.wireOp",EDGE,"E3.left")])]});
            var Q18;
            Q18=makeQuery(id+"F1.opExtrude","CAP_EDGE",EDGE,{"disambiguationData":[OSD([sQuery(id+"F0.wireOp",EDGE,"E3.top")])],"isStart":false});
            var Q19;
            Q19=makeQuery(id+"F1.opExtrude","CAP_EDGE",EDGE,{"disambiguationData":[OSD([sQuery(id+"F0.wireOp",EDGE,"E3.top")])],"isStart":true});
            var Q20;
            Q20=makeQuery(id+"F1.opExtrude","SWEPT_EDGE",EDGE,{"disambiguationData":[OSD([sQuery(id+"F0.wireOp",EDGE,"E0.top"),sQuery(id+"F0.wireOp",EDGE,"E0.left")])]});
            var Q21;
            Q21=makeQuery(id+"F1.opExtrude","CAP_EDGE",EDGE,{"disambiguationData":[OSD([sQuery(id+"F0.wireOp",EDGE,"E0.top")])],"isStart":false});
            var Q22;
            Q22=makeQuery(id+"F1.opExtrude","SWEPT_EDGE",EDGE,{"disambiguationData":[OSD([sQuery(id+"F0.wireOp",EDGE,"E0.top"),sQuery(id+"F0.wireOp",EDGE,"E0.right")])]});
            var Q23;
            Q23=makeQuery(id+"F1.opExtrude","CAP_EDGE",EDGE,{"disambiguationData":[OSD([sQuery(id+"F0.wireOp",EDGE,"E0.top")])],"isStart":true});
            var Q24;
            Q24=makeQuery(id+"F1.opExtrude","CAP_EDGE",EDGE,{"disambiguationData":[OSD([sQuery(id+"F0.wireOp",EDGE,"E4.left")])],"isStart":true});
            var Q25;
            Q25=makeQuery(id+"F1.opExtrude","CAP_EDGE",EDGE,{"disambiguationData":[OSD([sQuery(id+"F0.wireOp",EDGE,"E4.left")])],"isStart":false});
            var Q26;
            Q26=makeQuery(id+"F1.opExtrude","SWEPT_EDGE",EDGE,{"disambiguationData":[OSD([sQuery(id+"F0.wireOp",EDGE,"E4.bottom"),sQuery(id+"F0.wireOp",EDGE,"E4.left")])]});
            var Q27;
            Q27=makeQuery(id+"F1.opExtrude","SWEPT_EDGE",EDGE,{"disambiguationData":[OSD([sQuery(id+"F0.wireOp",EDGE,"E4.top"),sQuery(id+"F0.wireOp",EDGE,"E4.left")])]});
            var Q28;
            Q28=makeQuery(id+"F1.opExtrude","CAP_EDGE",EDGE,{"disambiguationData":[OSD([sQuery(id+"F0.wireOp",EDGE,"E1.left")])],"isStart":true});
            var Q29;
            Q29=makeQuery(id+"F1.opExtrude","CAP_EDGE",EDGE,{"disambiguationData":[OSD([sQuery(id+"F0.wireOp",EDGE,"E1.left")])],"isStart":false});
            var Q30;
            Q30=makeQuery(id+"F1.opExtrude","SWEPT_EDGE",EDGE,{"disambiguationData":[OSD([sQuery(id+"F0.wireOp",EDGE,"E1.top"),sQuery(id+"F0.wireOp",EDGE,"E1.left")])]});
            var Q31;
            Q31=makeQuery(id+"F1.opExtrude","SWEPT_EDGE",EDGE,{"disambiguationData":[OSD([sQuery(id+"F0.wireOp",EDGE,"E1.bottom"),sQuery(id+"F0.wireOp",EDGE,"E1.left")])]});
            fillet(context, id + "F4", {"entities" : qUnion([Q0, Q1, Q2, Q3, Q4, Q5, Q6, Q7, Q8, Q9, Q10, Q11, Q12, Q13, Q14, Q15, Q16, Q17, Q18, Q19, Q20, Q21, Q22, Q23, Q24, Q25, Q26, Q27, Q28, Q29, Q30, Q31]), "radius" : 1 * mm, "tangentPropagation" : true, "allowEdgeOverflow" : false});
        }
    });
